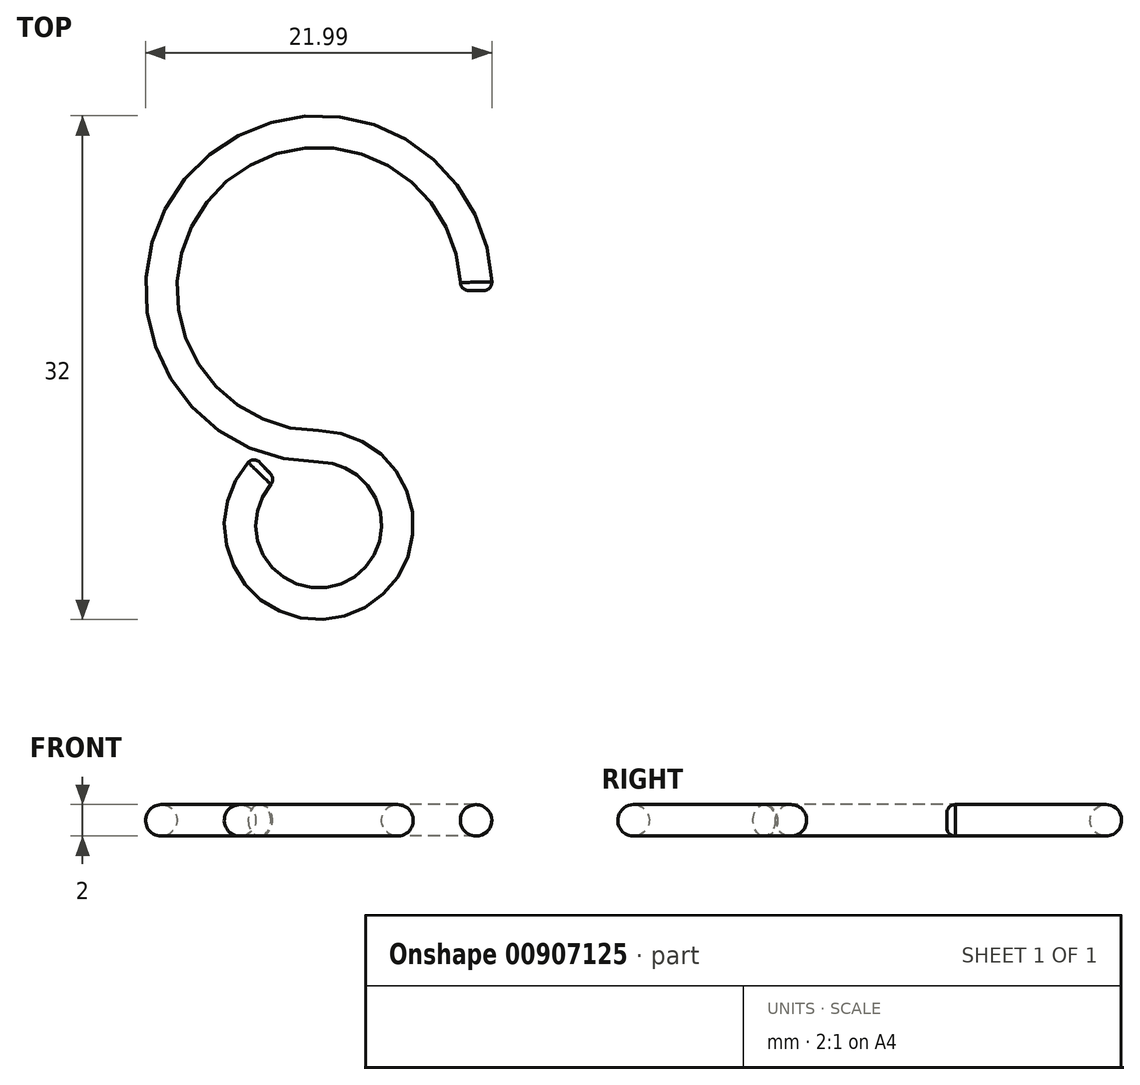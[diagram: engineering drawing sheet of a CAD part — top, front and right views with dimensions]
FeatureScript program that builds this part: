
annotation { "Feature Type Name" : "Feature", "Feature Type Description" : "" }
export const myFeature = defineFeature(function(context is Context, id is Id, definition is map)
    precondition{}
    {
        {
            var Q0;
            Q0=qCreatedBy(makeId("Top.planeOp"),FACE);
            var sketch = newSketch(context, id + "F0", { "sketchPlane" : qUnion([Q0])});
            skArc(sketch, "E0", {"start": v(10, 9.9) * mm, "mid": v(-7.04, 17.1) * mm, "end": v(0, 0) * mm});
            skArc(sketch, "E1", {"start": v(-3.43, -1.36) * mm, "mid": v(1.84, -9.65) * mm, "end": v(0, 0) * mm});
            skSolve(sketch);
        }
        {
            var Q0;
            Q0=qCreatedBy(makeId("Right.planeOp"),FACE);
            var sketch = newSketch(context, id + "F1", { "sketchPlane" : qUnion([Q0])});
            skCircle(sketch, "E2", {"center": v(0, 0) * mm, "radius": 1 * mm});
            skSolve(sketch);
        }
        {
            var Q0;
            Q0=makeQuery(id+"F1.imprint","IMPRINT",FACE,{"disambiguationData":[TD([[makeQuery(id+"F1.imprint","IMPRINT",EDGE,{"derivedFrom":sQuery(id+"F1.wireOp",EDGE,"E2")}),1.0]])]});
            var Q1;
            Q1 = qSketchRegion(id + "F0", true);
            var Q2;
            Q2=sQuery(id+"F1.wireOp",EDGE,"E2");
            var Q3;
            Q3=sQuery(id+"F0.wireOp",EDGE,"E0");
            var Q4;
            Q4=sQuery(id+"F0.wireOp",EDGE,"E1");
            sweep(context, id + "F2", {"profiles" : qUnion([Q0, Q1]), "surfaceProfiles" : qUnion([Q2]), "path" : qUnion([Q3, Q4])});
        }
        {
            var Q0;
            Q0=makeQuery(id+"F2.opSweep","CAP_EDGE",EDGE,{"disambiguationData":[OSD([sQuery(id+"F0.wireOp",VERTEX,"E1.start"),sQuery(id+"F1.wireOp",EDGE,"E2")])],"isStart":false});
            fillet(context, id + "F3", {"entities" : qUnion([Q0]), "radius" : 0.48 * mm, "tangentPropagation" : true, "allowEdgeOverflow" : false});
        }
        {
            var Q0;
            Q0=makeQuery(id+"F2.opSweep","CAP_FACE",FACE,{"disambiguationData":[OSD([sQuery(id+"F0.wireOp",VERTEX,"E0.start"),sQuery(id+"F1.wireOp",EDGE,"E2")])],"isStart":true});
            fillet(context, id + "F4", {"entities" : qUnion([Q0]), "radius" : 0.53 * mm, "tangentPropagation" : true, "allowEdgeOverflow" : false});
        }
    });
